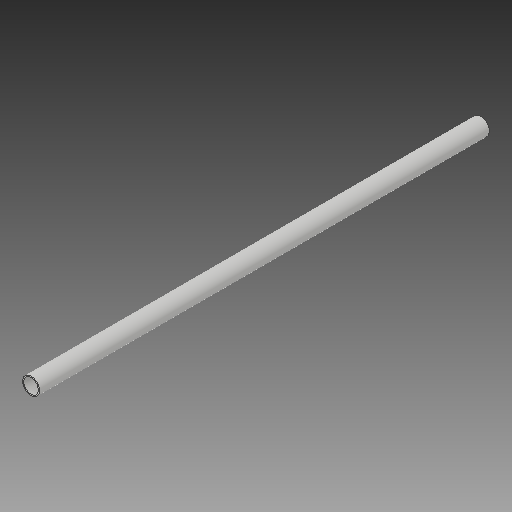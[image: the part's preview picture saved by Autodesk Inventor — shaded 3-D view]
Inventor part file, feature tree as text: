
AUTODESK INVENTOR PART (.ipt)
format: ipt  version: 2018.3 (Build 223284000, 284)  size: 79,872 bytes
history: native  units: mm
features: other x1, extrude x1, sketch x1
ambient origin geometry x8: Origin, YZ Plane, XZ Plane, XY Plane, X Axis, Y Axis, Z Axis, Center Point
bodies: Body1 (feature_tree)
feature tree (3):
  other  "ソリッド1"
  extrude  "押し出し1"  Depth=16.0mm
  sketch  "スケッチ1"
